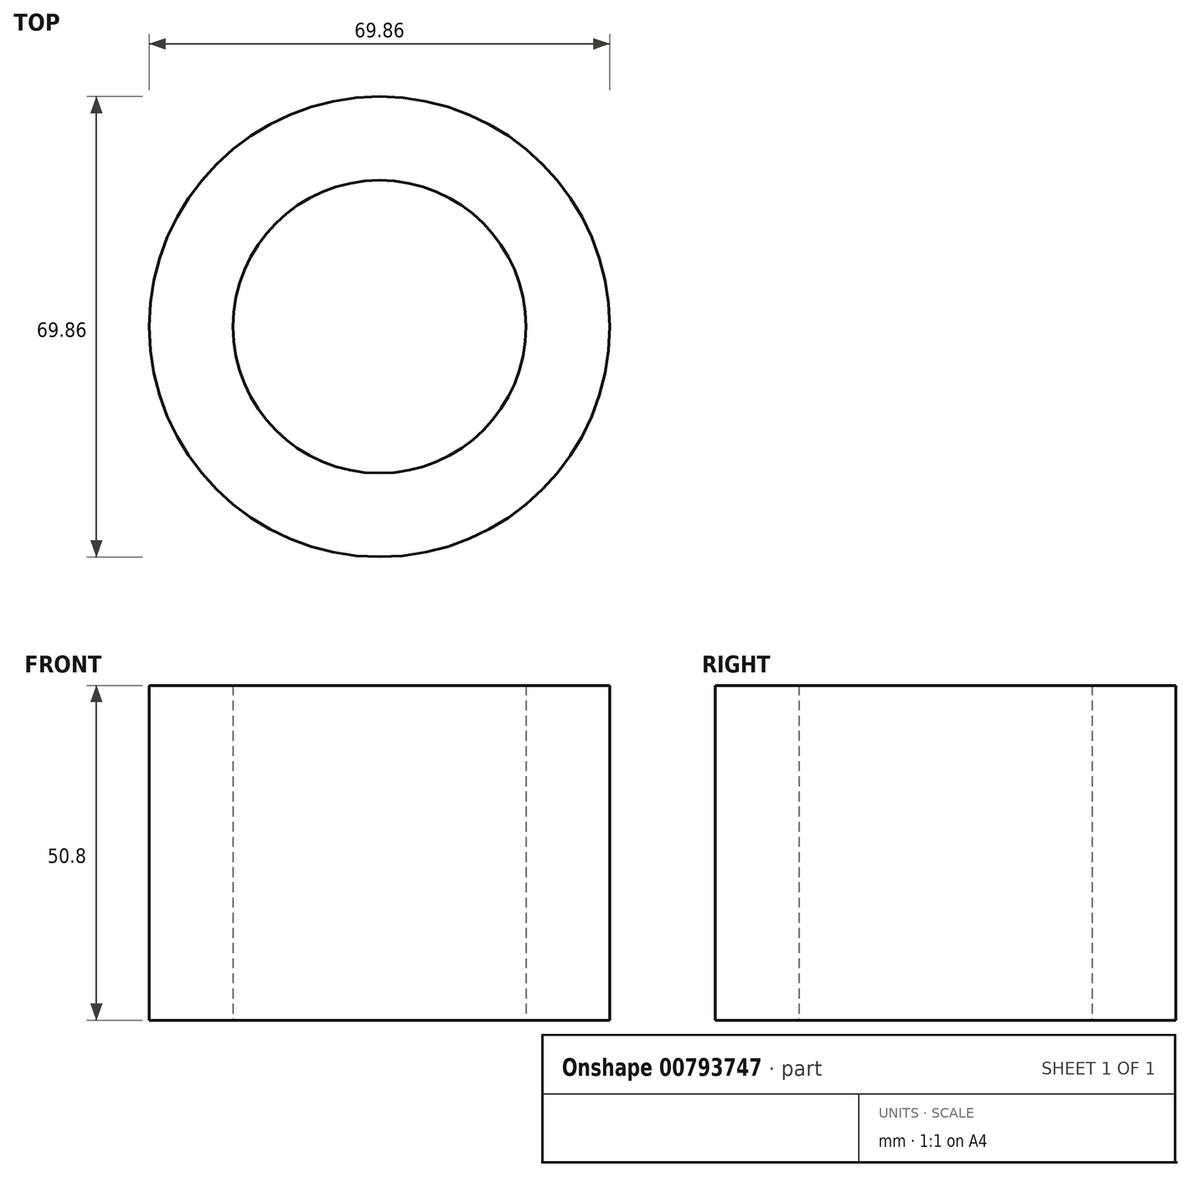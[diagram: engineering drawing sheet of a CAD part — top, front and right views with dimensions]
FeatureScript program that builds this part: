
annotation { "Feature Type Name" : "Feature", "Feature Type Description" : "" }
export const myFeature = defineFeature(function(context is Context, id is Id, definition is map)
    precondition{}
    {
        {
            var Q0;
            Q0=qCreatedBy(makeId("Top.planeOp"),FACE);
            var sketch = newSketch(context, id + "F0", { "sketchPlane" : qUnion([Q0])});
            skCircle(sketch, "E0", {"center": v(0, 0) * mm, "radius": 34.93 * mm});
            skCircle(sketch, "E1", {"center": v(0, 0) * mm, "radius": 22.23 * mm});
            skSolve(sketch);
        }
        {
            var Q0;
            Q0=makeQuery(id+"F0.imprint","IMPRINT",FACE,{"disambiguationData":[TD([[makeQuery(id+"F0.imprint","IMPRINT",EDGE,{"derivedFrom":sQuery(id+"F0.wireOp",EDGE,"E0")}),1.0]])]});
            extrude(context, id + "F1", {"entities" : qUnion([Q0]), "depth" : 50.8 * mm, "offsetDistance" : 25.4 * mm});
        }
    });
